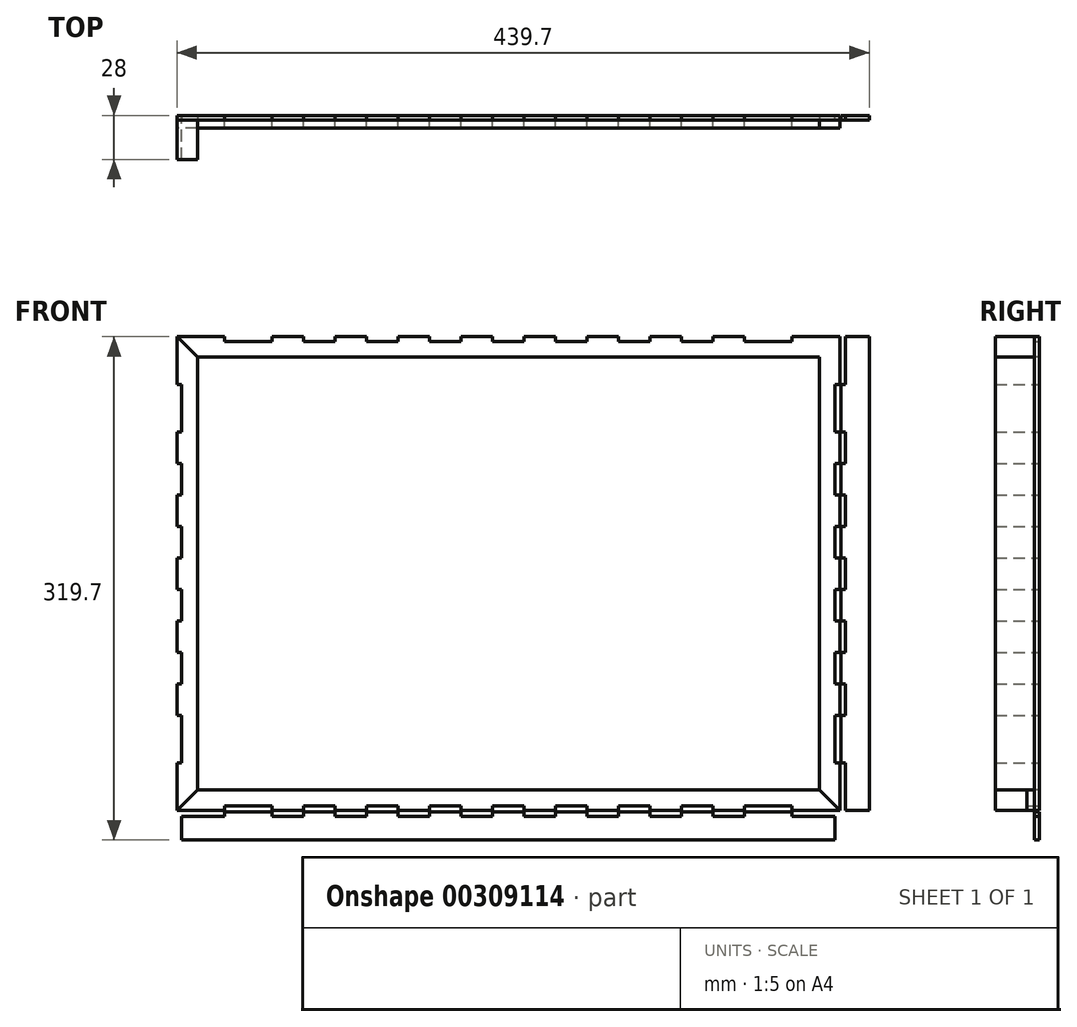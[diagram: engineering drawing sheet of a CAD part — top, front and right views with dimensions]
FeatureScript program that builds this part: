
annotation { "Feature Type Name" : "Feature", "Feature Type Description" : "" }
export const myFeature = defineFeature(function(context is Context, id is Id, definition is map)
    precondition{}
    {
        {
            var Q0;
            Q0=qCreatedBy(makeId("Front.planeOp"),FACE);
            var sketch = newSketch(context, id + "F0", { "sketchPlane" : qUnion([Q0])});
            skLineSegment(sketch, "E0", {"start": v(-313.85, 253.85) * mm, "end": v(-283.6, 253.85) * mm});
            skLineSegment(sketch, "E1", {"start": v(-283.6, 253.85) * mm, "end": v(-283.6, 250.85) * mm});
            skLineSegment(sketch, "E2", {"start": v(-283.6, 250.85) * mm, "end": v(-253.35, 250.85) * mm});
            skLineSegment(sketch, "E3", {"start": v(-253.35, 250.85) * mm, "end": v(-253.35, 253.85) * mm});
            skLineSegment(sketch, "E4", {"start": v(-253.35, 253.85) * mm, "end": v(-233.35, 253.85) * mm});
            skLineSegment(sketch, "E5", {"start": v(-233.35, 253.85) * mm, "end": v(-233.35, 250.85) * mm});
            skLineSegment(sketch, "E6", {"start": v(-233.35, 250.85) * mm, "end": v(-213.35, 250.85) * mm});
            skLineSegment(sketch, "E7", {"start": v(-213.35, 250.85) * mm, "end": v(-213.35, 253.85) * mm});
            skLineSegment(sketch, "E8", {"start": v(-213.35, 253.85) * mm, "end": v(-193.35, 253.85) * mm});
            skLineSegment(sketch, "E9", {"start": v(-193.35, 253.85) * mm, "end": v(-193.35, 250.85) * mm});
            skLineSegment(sketch, "E10", {"start": v(-193.35, 250.85) * mm, "end": v(-173.35, 250.85) * mm});
            skLineSegment(sketch, "E11", {"start": v(-173.35, 250.85) * mm, "end": v(-173.35, 253.85) * mm});
            skLineSegment(sketch, "E12", {"start": v(-173.35, 253.85) * mm, "end": v(-153.35, 253.85) * mm});
            skLineSegment(sketch, "E13", {"start": v(-153.35, 253.85) * mm, "end": v(-153.35, 250.85) * mm});
            skLineSegment(sketch, "E14", {"start": v(-153.35, 250.85) * mm, "end": v(-133.35, 250.85) * mm});
            skLineSegment(sketch, "E15", {"start": v(-133.35, 250.85) * mm, "end": v(-133.35, 253.85) * mm});
            skLineSegment(sketch, "E16", {"start": v(-133.35, 253.85) * mm, "end": v(-113.35, 253.85) * mm});
            skLineSegment(sketch, "E17", {"start": v(-113.35, 253.85) * mm, "end": v(-113.35, 250.85) * mm});
            skLineSegment(sketch, "E18", {"start": v(-113.35, 250.85) * mm, "end": v(-93.35, 250.85) * mm});
            skLineSegment(sketch, "E19", {"start": v(-93.35, 250.85) * mm, "end": v(-93.35, 253.85) * mm});
            skLineSegment(sketch, "E20", {"start": v(-93.35, 253.85) * mm, "end": v(-73.35, 253.85) * mm});
            skLineSegment(sketch, "E21", {"start": v(-73.35, 253.85) * mm, "end": v(-73.35, 250.85) * mm});
            skLineSegment(sketch, "E22", {"start": v(-73.35, 250.85) * mm, "end": v(-53.35, 250.85) * mm});
            skLineSegment(sketch, "E23", {"start": v(-53.35, 250.85) * mm, "end": v(-53.35, 253.85) * mm});
            skLineSegment(sketch, "E24", {"start": v(-53.35, 253.85) * mm, "end": v(-33.35, 253.85) * mm});
            skLineSegment(sketch, "E25", {"start": v(-33.35, 253.85) * mm, "end": v(-33.35, 250.85) * mm});
            skLineSegment(sketch, "E26", {"start": v(-33.35, 250.85) * mm, "end": v(-13.35, 250.85) * mm});
            skLineSegment(sketch, "E27", {"start": v(-13.35, 250.85) * mm, "end": v(-13.35, 253.85) * mm});
            skLineSegment(sketch, "E28", {"start": v(-13.35, 253.85) * mm, "end": v(6.65, 253.85) * mm});
            skLineSegment(sketch, "E29", {"start": v(6.65, 253.85) * mm, "end": v(6.65, 250.85) * mm});
            skLineSegment(sketch, "E30", {"start": v(6.65, 250.85) * mm, "end": v(26.65, 250.85) * mm});
            skLineSegment(sketch, "E31", {"start": v(26.65, 250.85) * mm, "end": v(26.65, 253.85) * mm});
            skLineSegment(sketch, "E32", {"start": v(26.65, 253.85) * mm, "end": v(46.65, 253.85) * mm});
            skLineSegment(sketch, "E33", {"start": v(46.65, 253.85) * mm, "end": v(46.65, 250.85) * mm});
            skLineSegment(sketch, "E34", {"start": v(46.65, 250.85) * mm, "end": v(76.9, 250.85) * mm});
            skLineSegment(sketch, "E35", {"start": v(76.9, 250.85) * mm, "end": v(76.9, 253.85) * mm});
            skLineSegment(sketch, "E36", {"start": v(76.9, 253.85) * mm, "end": v(107.15, 253.85) * mm});
            skLineSegment(sketch, "E37", {"start": v(107.15, 253.85) * mm, "end": v(107.15, 223.6) * mm});
            skLineSegment(sketch, "E38", {"start": v(107.15, 223.6) * mm, "end": v(104.15, 223.6) * mm});
            skLineSegment(sketch, "E39", {"start": v(104.15, 223.6) * mm, "end": v(104.15, 193.35) * mm});
            skLineSegment(sketch, "E40", {"start": v(104.15, 193.35) * mm, "end": v(107.15, 193.35) * mm});
            skLineSegment(sketch, "E41", {"start": v(107.15, 193.35) * mm, "end": v(107.15, 173.35) * mm});
            skLineSegment(sketch, "E42", {"start": v(107.15, 173.35) * mm, "end": v(104.15, 173.35) * mm});
            skLineSegment(sketch, "E43", {"start": v(104.15, 173.35) * mm, "end": v(104.15, 153.35) * mm});
            skLineSegment(sketch, "E44", {"start": v(104.15, 153.35) * mm, "end": v(107.15, 153.35) * mm});
            skLineSegment(sketch, "E45", {"start": v(107.15, 153.35) * mm, "end": v(107.15, 133.35) * mm});
            skLineSegment(sketch, "E46", {"start": v(107.15, 133.35) * mm, "end": v(104.15, 133.35) * mm});
            skLineSegment(sketch, "E47", {"start": v(104.15, 133.35) * mm, "end": v(104.15, 113.35) * mm});
            skLineSegment(sketch, "E48", {"start": v(104.15, 113.35) * mm, "end": v(107.15, 113.35) * mm});
            skLineSegment(sketch, "E49", {"start": v(107.15, 113.35) * mm, "end": v(107.15, 93.35) * mm});
            skLineSegment(sketch, "E50", {"start": v(107.15, 93.35) * mm, "end": v(104.15, 93.35) * mm});
            skLineSegment(sketch, "E51", {"start": v(104.15, 93.35) * mm, "end": v(104.15, 73.35) * mm});
            skLineSegment(sketch, "E52", {"start": v(104.15, 73.35) * mm, "end": v(107.15, 73.35) * mm});
            skLineSegment(sketch, "E53", {"start": v(107.15, 73.35) * mm, "end": v(107.15, 53.35) * mm});
            skLineSegment(sketch, "E54", {"start": v(107.15, 53.35) * mm, "end": v(104.15, 53.35) * mm});
            skLineSegment(sketch, "E55", {"start": v(104.15, 53.35) * mm, "end": v(104.15, 33.35) * mm});
            skLineSegment(sketch, "E56", {"start": v(104.15, 33.35) * mm, "end": v(107.15, 33.35) * mm});
            skLineSegment(sketch, "E57", {"start": v(107.15, 33.35) * mm, "end": v(107.15, 13.35) * mm});
            skLineSegment(sketch, "E58", {"start": v(107.15, 13.35) * mm, "end": v(104.15, 13.35) * mm});
            skLineSegment(sketch, "E59", {"start": v(104.15, 13.35) * mm, "end": v(104.15, -16.9) * mm});
            skLineSegment(sketch, "E60", {"start": v(104.15, -16.9) * mm, "end": v(107.15, -16.9) * mm});
            skLineSegment(sketch, "E61", {"start": v(107.15, -16.9) * mm, "end": v(107.15, -47.15) * mm});
            skLineSegment(sketch, "E62", {"start": v(107.15, -47.15) * mm, "end": v(76.9, -47.15) * mm});
            skLineSegment(sketch, "E63", {"start": v(76.9, -47.15) * mm, "end": v(76.9, -44.15) * mm});
            skLineSegment(sketch, "E64", {"start": v(76.9, -44.15) * mm, "end": v(46.65, -44.15) * mm});
            skLineSegment(sketch, "E65", {"start": v(46.65, -44.15) * mm, "end": v(46.65, -47.15) * mm});
            skLineSegment(sketch, "E66", {"start": v(46.65, -47.15) * mm, "end": v(26.65, -47.15) * mm});
            skLineSegment(sketch, "E67", {"start": v(26.65, -47.15) * mm, "end": v(26.65, -44.15) * mm});
            skLineSegment(sketch, "E68", {"start": v(26.65, -44.15) * mm, "end": v(6.65, -44.15) * mm});
            skLineSegment(sketch, "E69", {"start": v(6.65, -44.15) * mm, "end": v(6.65, -47.15) * mm});
            skLineSegment(sketch, "E70", {"start": v(6.65, -47.15) * mm, "end": v(-13.35, -47.15) * mm});
            skLineSegment(sketch, "E71", {"start": v(-13.35, -47.15) * mm, "end": v(-13.35, -44.15) * mm});
            skLineSegment(sketch, "E72", {"start": v(-13.35, -44.15) * mm, "end": v(-33.35, -44.15) * mm});
            skLineSegment(sketch, "E73", {"start": v(-33.35, -44.15) * mm, "end": v(-33.35, -47.15) * mm});
            skLineSegment(sketch, "E74", {"start": v(-33.35, -47.15) * mm, "end": v(-53.35, -47.15) * mm});
            skLineSegment(sketch, "E75", {"start": v(-53.35, -47.15) * mm, "end": v(-53.35, -44.15) * mm});
            skLineSegment(sketch, "E76", {"start": v(-53.35, -44.15) * mm, "end": v(-73.35, -44.15) * mm});
            skLineSegment(sketch, "E77", {"start": v(-73.35, -44.15) * mm, "end": v(-73.35, -47.15) * mm});
            skLineSegment(sketch, "E78", {"start": v(-73.35, -47.15) * mm, "end": v(-93.35, -47.15) * mm});
            skLineSegment(sketch, "E79", {"start": v(-93.35, -47.15) * mm, "end": v(-93.35, -44.15) * mm});
            skLineSegment(sketch, "E80", {"start": v(-93.35, -44.15) * mm, "end": v(-113.35, -44.15) * mm});
            skLineSegment(sketch, "E81", {"start": v(-113.35, -44.15) * mm, "end": v(-113.35, -47.15) * mm});
            skLineSegment(sketch, "E82", {"start": v(-113.35, -47.15) * mm, "end": v(-133.35, -47.15) * mm});
            skLineSegment(sketch, "E83", {"start": v(-133.35, -47.15) * mm, "end": v(-133.35, -44.15) * mm});
            skLineSegment(sketch, "E84", {"start": v(-133.35, -44.15) * mm, "end": v(-153.35, -44.15) * mm});
            skLineSegment(sketch, "E85", {"start": v(-153.35, -44.15) * mm, "end": v(-153.35, -47.15) * mm});
            skLineSegment(sketch, "E86", {"start": v(-153.35, -47.15) * mm, "end": v(-173.35, -47.15) * mm});
            skLineSegment(sketch, "E87", {"start": v(-173.35, -47.15) * mm, "end": v(-173.35, -44.15) * mm});
            skLineSegment(sketch, "E88", {"start": v(-173.35, -44.15) * mm, "end": v(-193.35, -44.15) * mm});
            skLineSegment(sketch, "E89", {"start": v(-193.35, -44.15) * mm, "end": v(-193.35, -47.15) * mm});
            skLineSegment(sketch, "E90", {"start": v(-193.35, -47.15) * mm, "end": v(-213.35, -47.15) * mm});
            skLineSegment(sketch, "E91", {"start": v(-213.35, -47.15) * mm, "end": v(-213.35, -44.15) * mm});
            skLineSegment(sketch, "E92", {"start": v(-213.35, -44.15) * mm, "end": v(-233.35, -44.15) * mm});
            skLineSegment(sketch, "E93", {"start": v(-233.35, -44.15) * mm, "end": v(-233.35, -47.15) * mm});
            skLineSegment(sketch, "E94", {"start": v(-233.35, -47.15) * mm, "end": v(-253.35, -47.15) * mm});
            skLineSegment(sketch, "E95", {"start": v(-253.35, -47.15) * mm, "end": v(-253.35, -44.15) * mm});
            skLineSegment(sketch, "E96", {"start": v(-253.35, -44.15) * mm, "end": v(-283.6, -44.15) * mm});
            skLineSegment(sketch, "E97", {"start": v(-283.6, -44.15) * mm, "end": v(-283.6, -47.15) * mm});
            skLineSegment(sketch, "E98", {"start": v(-283.6, -47.15) * mm, "end": v(-313.85, -47.15) * mm});
            skLineSegment(sketch, "E99", {"start": v(-313.85, -47.15) * mm, "end": v(-313.85, -16.9) * mm});
            skLineSegment(sketch, "E100", {"start": v(-313.85, -16.9) * mm, "end": v(-310.85, -16.9) * mm});
            skLineSegment(sketch, "E101", {"start": v(-310.85, -16.9) * mm, "end": v(-310.85, 13.35) * mm});
            skLineSegment(sketch, "E102", {"start": v(-310.85, 13.35) * mm, "end": v(-313.85, 13.35) * mm});
            skLineSegment(sketch, "E103", {"start": v(-313.85, 13.35) * mm, "end": v(-313.85, 33.35) * mm});
            skLineSegment(sketch, "E104", {"start": v(-313.85, 33.35) * mm, "end": v(-310.85, 33.35) * mm});
            skLineSegment(sketch, "E105", {"start": v(-310.85, 33.35) * mm, "end": v(-310.85, 53.35) * mm});
            skLineSegment(sketch, "E106", {"start": v(-310.85, 53.35) * mm, "end": v(-313.85, 53.35) * mm});
            skLineSegment(sketch, "E107", {"start": v(-313.85, 53.35) * mm, "end": v(-313.85, 73.35) * mm});
            skLineSegment(sketch, "E108", {"start": v(-313.85, 73.35) * mm, "end": v(-310.85, 73.35) * mm});
            skLineSegment(sketch, "E109", {"start": v(-310.85, 73.35) * mm, "end": v(-310.85, 93.35) * mm});
            skLineSegment(sketch, "E110", {"start": v(-310.85, 93.35) * mm, "end": v(-313.85, 93.35) * mm});
            skLineSegment(sketch, "E111", {"start": v(-313.85, 93.35) * mm, "end": v(-313.85, 113.35) * mm});
            skLineSegment(sketch, "E112", {"start": v(-313.85, 113.35) * mm, "end": v(-310.85, 113.35) * mm});
            skLineSegment(sketch, "E113", {"start": v(-310.85, 113.35) * mm, "end": v(-310.85, 133.35) * mm});
            skLineSegment(sketch, "E114", {"start": v(-310.85, 133.35) * mm, "end": v(-313.85, 133.35) * mm});
            skLineSegment(sketch, "E115", {"start": v(-313.85, 133.35) * mm, "end": v(-313.85, 153.35) * mm});
            skLineSegment(sketch, "E116", {"start": v(-313.85, 153.35) * mm, "end": v(-310.85, 153.35) * mm});
            skLineSegment(sketch, "E117", {"start": v(-310.85, 153.35) * mm, "end": v(-310.85, 173.35) * mm});
            skLineSegment(sketch, "E118", {"start": v(-310.85, 173.35) * mm, "end": v(-313.85, 173.35) * mm});
            skLineSegment(sketch, "E119", {"start": v(-313.85, 173.35) * mm, "end": v(-313.85, 193.35) * mm});
            skLineSegment(sketch, "E120", {"start": v(-313.85, 193.35) * mm, "end": v(-310.85, 193.35) * mm});
            skLineSegment(sketch, "E121", {"start": v(-310.85, 193.35) * mm, "end": v(-310.85, 223.6) * mm});
            skLineSegment(sketch, "E122", {"start": v(-310.85, 223.6) * mm, "end": v(-313.85, 223.6) * mm});
            skLineSegment(sketch, "E123", {"start": v(-313.85, 223.6) * mm, "end": v(-313.85, 253.85) * mm});
            skLineSegment(sketch, "E124", {"start": v(110.85, 253.85) * mm, "end": v(134.35, 253.85) * mm});
            skLineSegment(sketch, "E125", {"start": v(134.35, 253.85) * mm, "end": v(134.35, 250.85) * mm});
            skLineSegment(sketch, "E126", {"start": v(134.35, 250.85) * mm, "end": v(160.85, 250.85) * mm});
            skLineSegment(sketch, "E127", {"start": v(160.85, 250.85) * mm, "end": v(160.85, 253.85) * mm});
            skLineSegment(sketch, "E128", {"start": v(160.85, 253.85) * mm, "end": v(180.85, 253.85) * mm});
            skLineSegment(sketch, "E129", {"start": v(180.85, 253.85) * mm, "end": v(180.85, 250.85) * mm});
            skLineSegment(sketch, "E130", {"start": v(180.85, 250.85) * mm, "end": v(200.85, 250.85) * mm});
            skLineSegment(sketch, "E131", {"start": v(200.85, 250.85) * mm, "end": v(200.85, 253.85) * mm});
            skLineSegment(sketch, "E132", {"start": v(200.85, 253.85) * mm, "end": v(220.85, 253.85) * mm});
            skLineSegment(sketch, "E133", {"start": v(220.85, 253.85) * mm, "end": v(220.85, 250.85) * mm});
            skLineSegment(sketch, "E134", {"start": v(220.85, 250.85) * mm, "end": v(240.85, 250.85) * mm});
            skLineSegment(sketch, "E135", {"start": v(240.85, 250.85) * mm, "end": v(240.85, 253.85) * mm});
            skLineSegment(sketch, "E136", {"start": v(240.85, 253.85) * mm, "end": v(260.85, 253.85) * mm});
            skLineSegment(sketch, "E137", {"start": v(260.85, 253.85) * mm, "end": v(260.85, 250.85) * mm});
            skLineSegment(sketch, "E138", {"start": v(260.85, 250.85) * mm, "end": v(287.35, 250.85) * mm});
            skLineSegment(sketch, "E139", {"start": v(287.35, 250.85) * mm, "end": v(287.35, 253.85) * mm});
            skLineSegment(sketch, "E140", {"start": v(287.35, 253.85) * mm, "end": v(310.85, 253.85) * mm});
            skLineSegment(sketch, "E141", {"start": v(310.85, 253.85) * mm, "end": v(310.85, 223.6) * mm});
            skLineSegment(sketch, "E142", {"start": v(310.85, 223.6) * mm, "end": v(313.85, 223.6) * mm});
            skLineSegment(sketch, "E143", {"start": v(313.85, 223.6) * mm, "end": v(313.85, 193.35) * mm});
            skLineSegment(sketch, "E144", {"start": v(313.85, 193.35) * mm, "end": v(310.85, 193.35) * mm});
            skLineSegment(sketch, "E145", {"start": v(310.85, 193.35) * mm, "end": v(310.85, 173.35) * mm});
            skLineSegment(sketch, "E146", {"start": v(310.85, 173.35) * mm, "end": v(313.85, 173.35) * mm});
            skLineSegment(sketch, "E147", {"start": v(313.85, 173.35) * mm, "end": v(313.85, 153.35) * mm});
            skLineSegment(sketch, "E148", {"start": v(313.85, 153.35) * mm, "end": v(310.85, 153.35) * mm});
            skLineSegment(sketch, "E149", {"start": v(310.85, 153.35) * mm, "end": v(310.85, 133.35) * mm});
            skLineSegment(sketch, "E150", {"start": v(310.85, 133.35) * mm, "end": v(313.85, 133.35) * mm});
            skLineSegment(sketch, "E151", {"start": v(313.85, 133.35) * mm, "end": v(313.85, 113.35) * mm});
            skLineSegment(sketch, "E152", {"start": v(313.85, 113.35) * mm, "end": v(310.85, 113.35) * mm});
            skLineSegment(sketch, "E153", {"start": v(310.85, 113.35) * mm, "end": v(310.85, 93.35) * mm});
            skLineSegment(sketch, "E154", {"start": v(310.85, 93.35) * mm, "end": v(313.85, 93.35) * mm});
            skLineSegment(sketch, "E155", {"start": v(313.85, 93.35) * mm, "end": v(313.85, 73.35) * mm});
            skLineSegment(sketch, "E156", {"start": v(313.85, 73.35) * mm, "end": v(310.85, 73.35) * mm});
            skLineSegment(sketch, "E157", {"start": v(310.85, 73.35) * mm, "end": v(310.85, 53.35) * mm});
            skLineSegment(sketch, "E158", {"start": v(310.85, 53.35) * mm, "end": v(313.85, 53.35) * mm});
            skLineSegment(sketch, "E159", {"start": v(313.85, 53.35) * mm, "end": v(313.85, 33.35) * mm});
            skLineSegment(sketch, "E160", {"start": v(313.85, 33.35) * mm, "end": v(310.85, 33.35) * mm});
            skLineSegment(sketch, "E161", {"start": v(310.85, 33.35) * mm, "end": v(310.85, 13.35) * mm});
            skLineSegment(sketch, "E162", {"start": v(310.85, 13.35) * mm, "end": v(313.85, 13.35) * mm});
            skLineSegment(sketch, "E163", {"start": v(313.85, 13.35) * mm, "end": v(313.85, -16.9) * mm});
            skLineSegment(sketch, "E164", {"start": v(313.85, -16.9) * mm, "end": v(310.85, -16.9) * mm});
            skLineSegment(sketch, "E165", {"start": v(310.85, -16.9) * mm, "end": v(310.85, -47.15) * mm});
            skLineSegment(sketch, "E166", {"start": v(310.85, -47.15) * mm, "end": v(287.35, -47.15) * mm});
            skLineSegment(sketch, "E167", {"start": v(287.35, -47.15) * mm, "end": v(287.35, -44.15) * mm});
            skLineSegment(sketch, "E168", {"start": v(287.35, -44.15) * mm, "end": v(260.85, -44.15) * mm});
            skLineSegment(sketch, "E169", {"start": v(260.85, -44.15) * mm, "end": v(260.85, -47.15) * mm});
            skLineSegment(sketch, "E170", {"start": v(260.85, -47.15) * mm, "end": v(240.85, -47.15) * mm});
            skLineSegment(sketch, "E171", {"start": v(240.85, -47.15) * mm, "end": v(240.85, -44.15) * mm});
            skLineSegment(sketch, "E172", {"start": v(240.85, -44.15) * mm, "end": v(220.85, -44.15) * mm});
            skLineSegment(sketch, "E173", {"start": v(220.85, -44.15) * mm, "end": v(220.85, -47.15) * mm});
            skLineSegment(sketch, "E174", {"start": v(220.85, -47.15) * mm, "end": v(200.85, -47.15) * mm});
            skLineSegment(sketch, "E175", {"start": v(200.85, -47.15) * mm, "end": v(200.85, -44.15) * mm});
            skLineSegment(sketch, "E176", {"start": v(200.85, -44.15) * mm, "end": v(180.85, -44.15) * mm});
            skLineSegment(sketch, "E177", {"start": v(180.85, -44.15) * mm, "end": v(180.85, -47.15) * mm});
            skLineSegment(sketch, "E178", {"start": v(180.85, -47.15) * mm, "end": v(160.85, -47.15) * mm});
            skLineSegment(sketch, "E179", {"start": v(160.85, -47.15) * mm, "end": v(160.85, -44.15) * mm});
            skLineSegment(sketch, "E180", {"start": v(160.85, -44.15) * mm, "end": v(134.35, -44.15) * mm});
            skLineSegment(sketch, "E181", {"start": v(134.35, -44.15) * mm, "end": v(134.35, -47.15) * mm});
            skLineSegment(sketch, "E182", {"start": v(134.35, -47.15) * mm, "end": v(110.85, -47.15) * mm});
            skLineSegment(sketch, "E183", {"start": v(110.85, -47.15) * mm, "end": v(110.85, -16.9) * mm});
            skLineSegment(sketch, "E184", {"start": v(110.85, -16.9) * mm, "end": v(107.85, -16.9) * mm});
            skLineSegment(sketch, "E185", {"start": v(107.85, -16.9) * mm, "end": v(107.85, 13.35) * mm});
            skLineSegment(sketch, "E186", {"start": v(107.85, 13.35) * mm, "end": v(110.85, 13.35) * mm});
            skLineSegment(sketch, "E187", {"start": v(110.85, 13.35) * mm, "end": v(110.85, 33.35) * mm});
            skLineSegment(sketch, "E188", {"start": v(110.85, 33.35) * mm, "end": v(107.85, 33.35) * mm});
            skLineSegment(sketch, "E189", {"start": v(107.85, 33.35) * mm, "end": v(107.85, 53.35) * mm});
            skLineSegment(sketch, "E190", {"start": v(107.85, 53.35) * mm, "end": v(110.85, 53.35) * mm});
            skLineSegment(sketch, "E191", {"start": v(110.85, 53.35) * mm, "end": v(110.85, 73.35) * mm});
            skLineSegment(sketch, "E192", {"start": v(110.85, 73.35) * mm, "end": v(107.85, 73.35) * mm});
            skLineSegment(sketch, "E193", {"start": v(107.85, 73.35) * mm, "end": v(107.85, 93.35) * mm});
            skLineSegment(sketch, "E194", {"start": v(107.85, 93.35) * mm, "end": v(110.85, 93.35) * mm});
            skLineSegment(sketch, "E195", {"start": v(110.85, 93.35) * mm, "end": v(110.85, 113.35) * mm});
            skLineSegment(sketch, "E196", {"start": v(110.85, 113.35) * mm, "end": v(107.85, 113.35) * mm});
            skLineSegment(sketch, "E197", {"start": v(107.85, 113.35) * mm, "end": v(107.85, 133.35) * mm});
            skLineSegment(sketch, "E198", {"start": v(107.85, 133.35) * mm, "end": v(110.85, 133.35) * mm});
            skLineSegment(sketch, "E199", {"start": v(110.85, 133.35) * mm, "end": v(110.85, 153.35) * mm});
            skLineSegment(sketch, "E200", {"start": v(110.85, 153.35) * mm, "end": v(107.85, 153.35) * mm});
            skLineSegment(sketch, "E201", {"start": v(107.85, 153.35) * mm, "end": v(107.85, 173.35) * mm});
            skLineSegment(sketch, "E202", {"start": v(107.85, 173.35) * mm, "end": v(110.85, 173.35) * mm});
            skLineSegment(sketch, "E203", {"start": v(110.85, 173.35) * mm, "end": v(110.85, 193.35) * mm});
            skLineSegment(sketch, "E204", {"start": v(110.85, 193.35) * mm, "end": v(107.85, 193.35) * mm});
            skLineSegment(sketch, "E205", {"start": v(107.85, 193.35) * mm, "end": v(107.85, 223.6) * mm});
            skLineSegment(sketch, "E206", {"start": v(107.85, 223.6) * mm, "end": v(110.85, 223.6) * mm});
            skLineSegment(sketch, "E207", {"start": v(110.85, 223.6) * mm, "end": v(110.85, 253.85) * mm});
            skLineSegment(sketch, "E208", {"start": v(-310.85, -50.85) * mm, "end": v(-283.6, -50.85) * mm});
            skLineSegment(sketch, "E209", {"start": v(-283.6, -50.85) * mm, "end": v(-283.6, -47.85) * mm});
            skLineSegment(sketch, "E210", {"start": v(-283.6, -47.85) * mm, "end": v(-253.35, -47.85) * mm});
            skLineSegment(sketch, "E211", {"start": v(-253.35, -47.85) * mm, "end": v(-253.35, -50.85) * mm});
            skLineSegment(sketch, "E212", {"start": v(-253.35, -50.85) * mm, "end": v(-233.35, -50.85) * mm});
            skLineSegment(sketch, "E213", {"start": v(-233.35, -50.85) * mm, "end": v(-233.35, -47.85) * mm});
            skLineSegment(sketch, "E214", {"start": v(-233.35, -47.85) * mm, "end": v(-213.35, -47.85) * mm});
            skLineSegment(sketch, "E215", {"start": v(-213.35, -47.85) * mm, "end": v(-213.35, -50.85) * mm});
            skLineSegment(sketch, "E216", {"start": v(-213.35, -50.85) * mm, "end": v(-193.35, -50.85) * mm});
            skLineSegment(sketch, "E217", {"start": v(-193.35, -50.85) * mm, "end": v(-193.35, -47.85) * mm});
            skLineSegment(sketch, "E218", {"start": v(-193.35, -47.85) * mm, "end": v(-173.35, -47.85) * mm});
            skLineSegment(sketch, "E219", {"start": v(-173.35, -47.85) * mm, "end": v(-173.35, -50.85) * mm});
            skLineSegment(sketch, "E220", {"start": v(-173.35, -50.85) * mm, "end": v(-153.35, -50.85) * mm});
            skLineSegment(sketch, "E221", {"start": v(-153.35, -50.85) * mm, "end": v(-153.35, -47.85) * mm});
            skLineSegment(sketch, "E222", {"start": v(-153.35, -47.85) * mm, "end": v(-133.35, -47.85) * mm});
            skLineSegment(sketch, "E223", {"start": v(-133.35, -47.85) * mm, "end": v(-133.35, -50.85) * mm});
            skLineSegment(sketch, "E224", {"start": v(-133.35, -50.85) * mm, "end": v(-113.35, -50.85) * mm});
            skLineSegment(sketch, "E225", {"start": v(-113.35, -50.85) * mm, "end": v(-113.35, -47.85) * mm});
            skLineSegment(sketch, "E226", {"start": v(-113.35, -47.85) * mm, "end": v(-93.35, -47.85) * mm});
            skLineSegment(sketch, "E227", {"start": v(-93.35, -47.85) * mm, "end": v(-93.35, -50.85) * mm});
            skLineSegment(sketch, "E228", {"start": v(-93.35, -50.85) * mm, "end": v(-73.35, -50.85) * mm});
            skLineSegment(sketch, "E229", {"start": v(-73.35, -50.85) * mm, "end": v(-73.35, -47.85) * mm});
            skLineSegment(sketch, "E230", {"start": v(-73.35, -47.85) * mm, "end": v(-53.35, -47.85) * mm});
            skLineSegment(sketch, "E231", {"start": v(-53.35, -47.85) * mm, "end": v(-53.35, -50.85) * mm});
            skLineSegment(sketch, "E232", {"start": v(-53.35, -50.85) * mm, "end": v(-33.35, -50.85) * mm});
            skLineSegment(sketch, "E233", {"start": v(-33.35, -50.85) * mm, "end": v(-33.35, -47.85) * mm});
            skLineSegment(sketch, "E234", {"start": v(-33.35, -47.85) * mm, "end": v(-13.35, -47.85) * mm});
            skLineSegment(sketch, "E235", {"start": v(-13.35, -47.85) * mm, "end": v(-13.35, -50.85) * mm});
            skLineSegment(sketch, "E236", {"start": v(-13.35, -50.85) * mm, "end": v(6.65, -50.85) * mm});
            skLineSegment(sketch, "E237", {"start": v(6.65, -50.85) * mm, "end": v(6.65, -47.85) * mm});
            skLineSegment(sketch, "E238", {"start": v(6.65, -47.85) * mm, "end": v(26.65, -47.85) * mm});
            skLineSegment(sketch, "E239", {"start": v(26.65, -47.85) * mm, "end": v(26.65, -50.85) * mm});
            skLineSegment(sketch, "E240", {"start": v(26.65, -50.85) * mm, "end": v(46.65, -50.85) * mm});
            skLineSegment(sketch, "E241", {"start": v(46.65, -50.85) * mm, "end": v(46.65, -47.85) * mm});
            skLineSegment(sketch, "E242", {"start": v(46.65, -47.85) * mm, "end": v(76.9, -47.85) * mm});
            skLineSegment(sketch, "E243", {"start": v(76.9, -47.85) * mm, "end": v(76.9, -50.85) * mm});
            skLineSegment(sketch, "E244", {"start": v(76.9, -50.85) * mm, "end": v(104.15, -50.85) * mm});
            skLineSegment(sketch, "E245", {"start": v(104.15, -50.85) * mm, "end": v(104.15, -74.35) * mm});
            skLineSegment(sketch, "E246", {"start": v(104.15, -74.35) * mm, "end": v(107.15, -74.35) * mm});
            skLineSegment(sketch, "E247", {"start": v(107.15, -74.35) * mm, "end": v(107.15, -100.85) * mm});
            skLineSegment(sketch, "E248", {"start": v(107.15, -100.85) * mm, "end": v(104.15, -100.85) * mm});
            skLineSegment(sketch, "E249", {"start": v(104.15, -100.85) * mm, "end": v(104.15, -120.85) * mm});
            skLineSegment(sketch, "E250", {"start": v(104.15, -120.85) * mm, "end": v(107.15, -120.85) * mm});
            skLineSegment(sketch, "E251", {"start": v(107.15, -120.85) * mm, "end": v(107.15, -140.85) * mm});
            skLineSegment(sketch, "E252", {"start": v(107.15, -140.85) * mm, "end": v(104.15, -140.85) * mm});
            skLineSegment(sketch, "E253", {"start": v(104.15, -140.85) * mm, "end": v(104.15, -160.85) * mm});
            skLineSegment(sketch, "E254", {"start": v(104.15, -160.85) * mm, "end": v(107.15, -160.85) * mm});
            skLineSegment(sketch, "E255", {"start": v(107.15, -160.85) * mm, "end": v(107.15, -180.85) * mm});
            skLineSegment(sketch, "E256", {"start": v(107.15, -180.85) * mm, "end": v(104.15, -180.85) * mm});
            skLineSegment(sketch, "E257", {"start": v(104.15, -180.85) * mm, "end": v(104.15, -200.85) * mm});
            skLineSegment(sketch, "E258", {"start": v(104.15, -200.85) * mm, "end": v(107.15, -200.85) * mm});
            skLineSegment(sketch, "E259", {"start": v(107.15, -200.85) * mm, "end": v(107.15, -227.35) * mm});
            skLineSegment(sketch, "E260", {"start": v(107.15, -227.35) * mm, "end": v(104.15, -227.35) * mm});
            skLineSegment(sketch, "E261", {"start": v(104.15, -227.35) * mm, "end": v(104.15, -250.85) * mm});
            skLineSegment(sketch, "E262", {"start": v(104.15, -250.85) * mm, "end": v(76.9, -250.85) * mm});
            skLineSegment(sketch, "E263", {"start": v(76.9, -250.85) * mm, "end": v(76.9, -253.85) * mm});
            skLineSegment(sketch, "E264", {"start": v(76.9, -253.85) * mm, "end": v(46.65, -253.85) * mm});
            skLineSegment(sketch, "E265", {"start": v(46.65, -253.85) * mm, "end": v(46.65, -250.85) * mm});
            skLineSegment(sketch, "E266", {"start": v(46.65, -250.85) * mm, "end": v(26.65, -250.85) * mm});
            skLineSegment(sketch, "E267", {"start": v(26.65, -250.85) * mm, "end": v(26.65, -253.85) * mm});
            skLineSegment(sketch, "E268", {"start": v(26.65, -253.85) * mm, "end": v(6.65, -253.85) * mm});
            skLineSegment(sketch, "E269", {"start": v(6.65, -253.85) * mm, "end": v(6.65, -250.85) * mm});
            skLineSegment(sketch, "E270", {"start": v(6.65, -250.85) * mm, "end": v(-13.35, -250.85) * mm});
            skLineSegment(sketch, "E271", {"start": v(-13.35, -250.85) * mm, "end": v(-13.35, -253.85) * mm});
            skLineSegment(sketch, "E272", {"start": v(-13.35, -253.85) * mm, "end": v(-33.35, -253.85) * mm});
            skLineSegment(sketch, "E273", {"start": v(-33.35, -253.85) * mm, "end": v(-33.35, -250.85) * mm});
            skLineSegment(sketch, "E274", {"start": v(-33.35, -250.85) * mm, "end": v(-53.35, -250.85) * mm});
            skLineSegment(sketch, "E275", {"start": v(-53.35, -250.85) * mm, "end": v(-53.35, -253.85) * mm});
            skLineSegment(sketch, "E276", {"start": v(-53.35, -253.85) * mm, "end": v(-73.35, -253.85) * mm});
            skLineSegment(sketch, "E277", {"start": v(-73.35, -253.85) * mm, "end": v(-73.35, -250.85) * mm});
            skLineSegment(sketch, "E278", {"start": v(-73.35, -250.85) * mm, "end": v(-93.35, -250.85) * mm});
            skLineSegment(sketch, "E279", {"start": v(-93.35, -250.85) * mm, "end": v(-93.35, -253.85) * mm});
            skLineSegment(sketch, "E280", {"start": v(-93.35, -253.85) * mm, "end": v(-113.35, -253.85) * mm});
            skLineSegment(sketch, "E281", {"start": v(-113.35, -253.85) * mm, "end": v(-113.35, -250.85) * mm});
            skLineSegment(sketch, "E282", {"start": v(-113.35, -250.85) * mm, "end": v(-133.35, -250.85) * mm});
            skLineSegment(sketch, "E283", {"start": v(-133.35, -250.85) * mm, "end": v(-133.35, -253.85) * mm});
            skLineSegment(sketch, "E284", {"start": v(-133.35, -253.85) * mm, "end": v(-153.35, -253.85) * mm});
            skLineSegment(sketch, "E285", {"start": v(-153.35, -253.85) * mm, "end": v(-153.35, -250.85) * mm});
            skLineSegment(sketch, "E286", {"start": v(-153.35, -250.85) * mm, "end": v(-173.35, -250.85) * mm});
            skLineSegment(sketch, "E287", {"start": v(-173.35, -250.85) * mm, "end": v(-173.35, -253.85) * mm});
            skLineSegment(sketch, "E288", {"start": v(-173.35, -253.85) * mm, "end": v(-193.35, -253.85) * mm});
            skLineSegment(sketch, "E289", {"start": v(-193.35, -253.85) * mm, "end": v(-193.35, -250.85) * mm});
            skLineSegment(sketch, "E290", {"start": v(-193.35, -250.85) * mm, "end": v(-213.35, -250.85) * mm});
            skLineSegment(sketch, "E291", {"start": v(-213.35, -250.85) * mm, "end": v(-213.35, -253.85) * mm});
            skLineSegment(sketch, "E292", {"start": v(-213.35, -253.85) * mm, "end": v(-233.35, -253.85) * mm});
            skLineSegment(sketch, "E293", {"start": v(-233.35, -253.85) * mm, "end": v(-233.35, -250.85) * mm});
            skLineSegment(sketch, "E294", {"start": v(-233.35, -250.85) * mm, "end": v(-253.35, -250.85) * mm});
            skLineSegment(sketch, "E295", {"start": v(-253.35, -250.85) * mm, "end": v(-253.35, -253.85) * mm});
            skLineSegment(sketch, "E296", {"start": v(-253.35, -253.85) * mm, "end": v(-283.6, -253.85) * mm});
            skLineSegment(sketch, "E297", {"start": v(-283.6, -253.85) * mm, "end": v(-283.6, -250.85) * mm});
            skLineSegment(sketch, "E298", {"start": v(-283.6, -250.85) * mm, "end": v(-310.85, -250.85) * mm});
            skLineSegment(sketch, "E299", {"start": v(-310.85, -250.85) * mm, "end": v(-310.85, -227.35) * mm});
            skLineSegment(sketch, "E300", {"start": v(-310.85, -227.35) * mm, "end": v(-313.85, -227.35) * mm});
            skLineSegment(sketch, "E301", {"start": v(-313.85, -227.35) * mm, "end": v(-313.85, -200.85) * mm});
            skLineSegment(sketch, "E302", {"start": v(-313.85, -200.85) * mm, "end": v(-310.85, -200.85) * mm});
            skLineSegment(sketch, "E303", {"start": v(-310.85, -200.85) * mm, "end": v(-310.85, -180.85) * mm});
            skLineSegment(sketch, "E304", {"start": v(-310.85, -180.85) * mm, "end": v(-313.85, -180.85) * mm});
            skLineSegment(sketch, "E305", {"start": v(-313.85, -180.85) * mm, "end": v(-313.85, -160.85) * mm});
            skLineSegment(sketch, "E306", {"start": v(-313.85, -160.85) * mm, "end": v(-310.85, -160.85) * mm});
            skLineSegment(sketch, "E307", {"start": v(-310.85, -160.85) * mm, "end": v(-310.85, -140.85) * mm});
            skLineSegment(sketch, "E308", {"start": v(-310.85, -140.85) * mm, "end": v(-313.85, -140.85) * mm});
            skLineSegment(sketch, "E309", {"start": v(-313.85, -140.85) * mm, "end": v(-313.85, -120.85) * mm});
            skLineSegment(sketch, "E310", {"start": v(-313.85, -120.85) * mm, "end": v(-310.85, -120.85) * mm});
            skLineSegment(sketch, "E311", {"start": v(-310.85, -120.85) * mm, "end": v(-310.85, -100.85) * mm});
            skLineSegment(sketch, "E312", {"start": v(-310.85, -100.85) * mm, "end": v(-313.85, -100.85) * mm});
            skLineSegment(sketch, "E313", {"start": v(-313.85, -100.85) * mm, "end": v(-313.85, -74.35) * mm});
            skLineSegment(sketch, "E314", {"start": v(-313.85, -74.35) * mm, "end": v(-310.85, -74.35) * mm});
            skLineSegment(sketch, "E315", {"start": v(-310.85, -74.35) * mm, "end": v(-310.85, -50.85) * mm});
            skSolve(sketch);
        }
        {
            var Q0;
            Q0 = qSketchRegion(id + "F0", true);
            extrude(context, id + "F1", {"entities" : qUnion([Q0]), "depth" : 3 * mm});
        }
        {
            var Q0;
            Q0=makeQuery(id+"F1.opExtrude","CAP_FACE",FACE,{"disambiguationData":[OSD([sQuery(id+"F0.wireOp",EDGE,"E0"),sQuery(id+"F0.wireOp",EDGE,"E1"),sQuery(id+"F0.wireOp",EDGE,"E2"),sQuery(id+"F0.wireOp",EDGE,"E3"),sQuery(id+"F0.wireOp",EDGE,"E4"),sQuery(id+"F0.wireOp",EDGE,"E5"),sQuery(id+"F0.wireOp",EDGE,"E6"),sQuery(id+"F0.wireOp",EDGE,"E7"),sQuery(id+"F0.wireOp",EDGE,"E8"),sQuery(id+"F0.wireOp",EDGE,"E9"),sQuery(id+"F0.wireOp",EDGE,"E10"),sQuery(id+"F0.wireOp",EDGE,"E11"),sQuery(id+"F0.wireOp",EDGE,"E12"),sQuery(id+"F0.wireOp",EDGE,"E13"),sQuery(id+"F0.wireOp",EDGE,"E14"),sQuery(id+"F0.wireOp",EDGE,"E15"),sQuery(id+"F0.wireOp",EDGE,"E16"),sQuery(id+"F0.wireOp",EDGE,"E17"),sQuery(id+"F0.wireOp",EDGE,"E18"),sQuery(id+"F0.wireOp",EDGE,"E19"),sQuery(id+"F0.wireOp",EDGE,"E20"),sQuery(id+"F0.wireOp",EDGE,"E21"),sQuery(id+"F0.wireOp",EDGE,"E22"),sQuery(id+"F0.wireOp",EDGE,"E23"),sQuery(id+"F0.wireOp",EDGE,"E24"),sQuery(id+"F0.wireOp",EDGE,"E25"),sQuery(id+"F0.wireOp",EDGE,"E26"),sQuery(id+"F0.wireOp",EDGE,"E27"),sQuery(id+"F0.wireOp",EDGE,"E28"),sQuery(id+"F0.wireOp",EDGE,"E29"),sQuery(id+"F0.wireOp",EDGE,"E30"),sQuery(id+"F0.wireOp",EDGE,"E31"),sQuery(id+"F0.wireOp",EDGE,"E32"),sQuery(id+"F0.wireOp",EDGE,"E33"),sQuery(id+"F0.wireOp",EDGE,"E34"),sQuery(id+"F0.wireOp",EDGE,"E35"),sQuery(id+"F0.wireOp",EDGE,"E36"),sQuery(id+"F0.wireOp",EDGE,"E37"),sQuery(id+"F0.wireOp",EDGE,"E38"),sQuery(id+"F0.wireOp",EDGE,"E39"),sQuery(id+"F0.wireOp",EDGE,"E40"),sQuery(id+"F0.wireOp",EDGE,"E41"),sQuery(id+"F0.wireOp",EDGE,"E42"),sQuery(id+"F0.wireOp",EDGE,"E43"),sQuery(id+"F0.wireOp",EDGE,"E44"),sQuery(id+"F0.wireOp",EDGE,"E45"),sQuery(id+"F0.wireOp",EDGE,"E46"),sQuery(id+"F0.wireOp",EDGE,"E47"),sQuery(id+"F0.wireOp",EDGE,"E48"),sQuery(id+"F0.wireOp",EDGE,"E49"),sQuery(id+"F0.wireOp",EDGE,"E50"),sQuery(id+"F0.wireOp",EDGE,"E51"),sQuery(id+"F0.wireOp",EDGE,"E52"),sQuery(id+"F0.wireOp",EDGE,"E53"),sQuery(id+"F0.wireOp",EDGE,"E54"),sQuery(id+"F0.wireOp",EDGE,"E55"),sQuery(id+"F0.wireOp",EDGE,"E56"),sQuery(id+"F0.wireOp",EDGE,"E57"),sQuery(id+"F0.wireOp",EDGE,"E58"),sQuery(id+"F0.wireOp",EDGE,"E59"),sQuery(id+"F0.wireOp",EDGE,"E60"),sQuery(id+"F0.wireOp",EDGE,"E61"),sQuery(id+"F0.wireOp",EDGE,"E62"),sQuery(id+"F0.wireOp",EDGE,"E63"),sQuery(id+"F0.wireOp",EDGE,"E64"),sQuery(id+"F0.wireOp",EDGE,"E65"),sQuery(id+"F0.wireOp",EDGE,"E66"),sQuery(id+"F0.wireOp",EDGE,"E67"),sQuery(id+"F0.wireOp",EDGE,"E68"),sQuery(id+"F0.wireOp",EDGE,"E69"),sQuery(id+"F0.wireOp",EDGE,"E70"),sQuery(id+"F0.wireOp",EDGE,"E71"),sQuery(id+"F0.wireOp",EDGE,"E72"),sQuery(id+"F0.wireOp",EDGE,"E73"),sQuery(id+"F0.wireOp",EDGE,"E74"),sQuery(id+"F0.wireOp",EDGE,"E75"),sQuery(id+"F0.wireOp",EDGE,"E76"),sQuery(id+"F0.wireOp",EDGE,"E77"),sQuery(id+"F0.wireOp",EDGE,"E78"),sQuery(id+"F0.wireOp",EDGE,"E79"),sQuery(id+"F0.wireOp",EDGE,"E80"),sQuery(id+"F0.wireOp",EDGE,"E81"),sQuery(id+"F0.wireOp",EDGE,"E82"),sQuery(id+"F0.wireOp",EDGE,"E83"),sQuery(id+"F0.wireOp",EDGE,"E84"),sQuery(id+"F0.wireOp",EDGE,"E85"),sQuery(id+"F0.wireOp",EDGE,"E86"),sQuery(id+"F0.wireOp",EDGE,"E87"),sQuery(id+"F0.wireOp",EDGE,"E88"),sQuery(id+"F0.wireOp",EDGE,"E89"),sQuery(id+"F0.wireOp",EDGE,"E90"),sQuery(id+"F0.wireOp",EDGE,"E91"),sQuery(id+"F0.wireOp",EDGE,"E92"),sQuery(id+"F0.wireOp",EDGE,"E93"),sQuery(id+"F0.wireOp",EDGE,"E94"),sQuery(id+"F0.wireOp",EDGE,"E95"),sQuery(id+"F0.wireOp",EDGE,"E96"),sQuery(id+"F0.wireOp",EDGE,"E97"),sQuery(id+"F0.wireOp",EDGE,"E98"),sQuery(id+"F0.wireOp",EDGE,"E99"),sQuery(id+"F0.wireOp",EDGE,"E100"),sQuery(id+"F0.wireOp",EDGE,"E101"),sQuery(id+"F0.wireOp",EDGE,"E102"),sQuery(id+"F0.wireOp",EDGE,"E103"),sQuery(id+"F0.wireOp",EDGE,"E104"),sQuery(id+"F0.wireOp",EDGE,"E105"),sQuery(id+"F0.wireOp",EDGE,"E106"),sQuery(id+"F0.wireOp",EDGE,"E107"),sQuery(id+"F0.wireOp",EDGE,"E108"),sQuery(id+"F0.wireOp",EDGE,"E109"),sQuery(id+"F0.wireOp",EDGE,"E110"),sQuery(id+"F0.wireOp",EDGE,"E111"),sQuery(id+"F0.wireOp",EDGE,"E112"),sQuery(id+"F0.wireOp",EDGE,"E113"),sQuery(id+"F0.wireOp",EDGE,"E114"),sQuery(id+"F0.wireOp",EDGE,"E115"),sQuery(id+"F0.wireOp",EDGE,"E116"),sQuery(id+"F0.wireOp",EDGE,"E117"),sQuery(id+"F0.wireOp",EDGE,"E118"),sQuery(id+"F0.wireOp",EDGE,"E119"),sQuery(id+"F0.wireOp",EDGE,"E120"),sQuery(id+"F0.wireOp",EDGE,"E121"),sQuery(id+"F0.wireOp",EDGE,"E122"),sQuery(id+"F0.wireOp",EDGE,"E123")])],"isStart":false});
            var sketch = newSketch(context, id + "F2", { "sketchPlane" : qUnion([Q0])});
            skLineSegment(sketch, "E316.bottom", {"start": v(-300.85, 240.85) * mm, "end": v(94.15, 240.85) * mm});
            skLineSegment(sketch, "E316.top", {"start": v(-300.85, -34.15) * mm, "end": v(94.15, -34.15) * mm});
            skLineSegment(sketch, "E316.left", {"start": v(-300.85, 240.85) * mm, "end": v(-300.85, -34.15) * mm});
            skLineSegment(sketch, "E316.right", {"start": v(94.15, 240.85) * mm, "end": v(94.15, -34.15) * mm});
            skLineSegment(sketch, "E317", {"start": v(-183.35, 250.85) * mm, "end": v(-183.35, 240.85) * mm, "construction": true});
            skLineSegment(sketch, "E318", {"start": v(-310.85, 123.35) * mm, "end": v(-300.85, 123.35) * mm, "construction": true});
            skLineSegment(sketch, "E319", {"start": v(-183.35, -44.15) * mm, "end": v(-183.35, -34.15) * mm, "construction": true});
            skLineSegment(sketch, "E320", {"start": v(104.15, 123.35) * mm, "end": v(94.15, 123.35) * mm, "construction": true});
            skLineSegment(sketch, "E321.bottom", {"start": v(313.85, 253.85) * mm, "end": v(125.85, 253.85) * mm});
            skLineSegment(sketch, "E321.top", {"start": v(313.85, -47.15) * mm, "end": v(125.85, -47.15) * mm});
            skLineSegment(sketch, "E321.left", {"start": v(313.85, 253.85) * mm, "end": v(313.85, -47.15) * mm});
            skLineSegment(sketch, "E321.right", {"start": v(125.85, 253.85) * mm, "end": v(125.85, -47.15) * mm});
            skLineSegment(sketch, "E322.bottom", {"start": v(-313.85, -253.85) * mm, "end": v(107.15, -253.85) * mm});
            skLineSegment(sketch, "E322.top", {"start": v(-313.85, -65.85) * mm, "end": v(107.15, -65.85) * mm});
            skLineSegment(sketch, "E322.left", {"start": v(-313.85, -253.85) * mm, "end": v(-313.85, -65.85) * mm});
            skLineSegment(sketch, "E322.right", {"start": v(107.15, -253.85) * mm, "end": v(107.15, -65.85) * mm});
            skLineSegment(sketch, "E323", {"start": v(125.85, 20.75) * mm, "end": v(110.85, 20.75) * mm, "construction": true});
            skLineSegment(sketch, "E324", {"start": v(39.3, -65.85) * mm, "end": v(39.3, -50.85) * mm, "construction": true});
            skSolve(sketch);
        }
        {
            var Q0;
            Q0 = qSketchRegion(id + "F2", true);
            extrude(context, id + "F3", {"entities" : qUnion([Q0]), "operationType" : NewBodyOperationType.REMOVE, "oppositeDirection" : true, "depth" : 25 * mm});
        }
        {
            var Q0;
            Q0=makeQuery(id+"F1.opExtrude","CAP_FACE",FACE,{"disambiguationData":[OSD([sQuery(id+"F0.wireOp",EDGE,"E0"),sQuery(id+"F0.wireOp",EDGE,"E1"),sQuery(id+"F0.wireOp",EDGE,"E2"),sQuery(id+"F0.wireOp",EDGE,"E3"),sQuery(id+"F0.wireOp",EDGE,"E4"),sQuery(id+"F0.wireOp",EDGE,"E5"),sQuery(id+"F0.wireOp",EDGE,"E6"),sQuery(id+"F0.wireOp",EDGE,"E7"),sQuery(id+"F0.wireOp",EDGE,"E8"),sQuery(id+"F0.wireOp",EDGE,"E9"),sQuery(id+"F0.wireOp",EDGE,"E10"),sQuery(id+"F0.wireOp",EDGE,"E11"),sQuery(id+"F0.wireOp",EDGE,"E12"),sQuery(id+"F0.wireOp",EDGE,"E13"),sQuery(id+"F0.wireOp",EDGE,"E14"),sQuery(id+"F0.wireOp",EDGE,"E15"),sQuery(id+"F0.wireOp",EDGE,"E16"),sQuery(id+"F0.wireOp",EDGE,"E17"),sQuery(id+"F0.wireOp",EDGE,"E18"),sQuery(id+"F0.wireOp",EDGE,"E19"),sQuery(id+"F0.wireOp",EDGE,"E20"),sQuery(id+"F0.wireOp",EDGE,"E21"),sQuery(id+"F0.wireOp",EDGE,"E22"),sQuery(id+"F0.wireOp",EDGE,"E23"),sQuery(id+"F0.wireOp",EDGE,"E24"),sQuery(id+"F0.wireOp",EDGE,"E25"),sQuery(id+"F0.wireOp",EDGE,"E26"),sQuery(id+"F0.wireOp",EDGE,"E27"),sQuery(id+"F0.wireOp",EDGE,"E28"),sQuery(id+"F0.wireOp",EDGE,"E29"),sQuery(id+"F0.wireOp",EDGE,"E30"),sQuery(id+"F0.wireOp",EDGE,"E31"),sQuery(id+"F0.wireOp",EDGE,"E32"),sQuery(id+"F0.wireOp",EDGE,"E33"),sQuery(id+"F0.wireOp",EDGE,"E34"),sQuery(id+"F0.wireOp",EDGE,"E35"),sQuery(id+"F0.wireOp",EDGE,"E36"),sQuery(id+"F0.wireOp",EDGE,"E37"),sQuery(id+"F0.wireOp",EDGE,"E38"),sQuery(id+"F0.wireOp",EDGE,"E39"),sQuery(id+"F0.wireOp",EDGE,"E40"),sQuery(id+"F0.wireOp",EDGE,"E41"),sQuery(id+"F0.wireOp",EDGE,"E42"),sQuery(id+"F0.wireOp",EDGE,"E43"),sQuery(id+"F0.wireOp",EDGE,"E44"),sQuery(id+"F0.wireOp",EDGE,"E45"),sQuery(id+"F0.wireOp",EDGE,"E46"),sQuery(id+"F0.wireOp",EDGE,"E47"),sQuery(id+"F0.wireOp",EDGE,"E48"),sQuery(id+"F0.wireOp",EDGE,"E49"),sQuery(id+"F0.wireOp",EDGE,"E50"),sQuery(id+"F0.wireOp",EDGE,"E51"),sQuery(id+"F0.wireOp",EDGE,"E52"),sQuery(id+"F0.wireOp",EDGE,"E53"),sQuery(id+"F0.wireOp",EDGE,"E54"),sQuery(id+"F0.wireOp",EDGE,"E55"),sQuery(id+"F0.wireOp",EDGE,"E56"),sQuery(id+"F0.wireOp",EDGE,"E57"),sQuery(id+"F0.wireOp",EDGE,"E58"),sQuery(id+"F0.wireOp",EDGE,"E59"),sQuery(id+"F0.wireOp",EDGE,"E60"),sQuery(id+"F0.wireOp",EDGE,"E61"),sQuery(id+"F0.wireOp",EDGE,"E62"),sQuery(id+"F0.wireOp",EDGE,"E63"),sQuery(id+"F0.wireOp",EDGE,"E64"),sQuery(id+"F0.wireOp",EDGE,"E65"),sQuery(id+"F0.wireOp",EDGE,"E66"),sQuery(id+"F0.wireOp",EDGE,"E67"),sQuery(id+"F0.wireOp",EDGE,"E68"),sQuery(id+"F0.wireOp",EDGE,"E69"),sQuery(id+"F0.wireOp",EDGE,"E70"),sQuery(id+"F0.wireOp",EDGE,"E71"),sQuery(id+"F0.wireOp",EDGE,"E72"),sQuery(id+"F0.wireOp",EDGE,"E73"),sQuery(id+"F0.wireOp",EDGE,"E74"),sQuery(id+"F0.wireOp",EDGE,"E75"),sQuery(id+"F0.wireOp",EDGE,"E76"),sQuery(id+"F0.wireOp",EDGE,"E77"),sQuery(id+"F0.wireOp",EDGE,"E78"),sQuery(id+"F0.wireOp",EDGE,"E79"),sQuery(id+"F0.wireOp",EDGE,"E80"),sQuery(id+"F0.wireOp",EDGE,"E81"),sQuery(id+"F0.wireOp",EDGE,"E82"),sQuery(id+"F0.wireOp",EDGE,"E83"),sQuery(id+"F0.wireOp",EDGE,"E84"),sQuery(id+"F0.wireOp",EDGE,"E85"),sQuery(id+"F0.wireOp",EDGE,"E86"),sQuery(id+"F0.wireOp",EDGE,"E87"),sQuery(id+"F0.wireOp",EDGE,"E88"),sQuery(id+"F0.wireOp",EDGE,"E89"),sQuery(id+"F0.wireOp",EDGE,"E90"),sQuery(id+"F0.wireOp",EDGE,"E91"),sQuery(id+"F0.wireOp",EDGE,"E92"),sQuery(id+"F0.wireOp",EDGE,"E93"),sQuery(id+"F0.wireOp",EDGE,"E94"),sQuery(id+"F0.wireOp",EDGE,"E95"),sQuery(id+"F0.wireOp",EDGE,"E96"),sQuery(id+"F0.wireOp",EDGE,"E97"),sQuery(id+"F0.wireOp",EDGE,"E98"),sQuery(id+"F0.wireOp",EDGE,"E99"),sQuery(id+"F0.wireOp",EDGE,"E100"),sQuery(id+"F0.wireOp",EDGE,"E101"),sQuery(id+"F0.wireOp",EDGE,"E102"),sQuery(id+"F0.wireOp",EDGE,"E103"),sQuery(id+"F0.wireOp",EDGE,"E104"),sQuery(id+"F0.wireOp",EDGE,"E105"),sQuery(id+"F0.wireOp",EDGE,"E106"),sQuery(id+"F0.wireOp",EDGE,"E107"),sQuery(id+"F0.wireOp",EDGE,"E108"),sQuery(id+"F0.wireOp",EDGE,"E109"),sQuery(id+"F0.wireOp",EDGE,"E110"),sQuery(id+"F0.wireOp",EDGE,"E111"),sQuery(id+"F0.wireOp",EDGE,"E112"),sQuery(id+"F0.wireOp",EDGE,"E113"),sQuery(id+"F0.wireOp",EDGE,"E114"),sQuery(id+"F0.wireOp",EDGE,"E115"),sQuery(id+"F0.wireOp",EDGE,"E116"),sQuery(id+"F0.wireOp",EDGE,"E117"),sQuery(id+"F0.wireOp",EDGE,"E118"),sQuery(id+"F0.wireOp",EDGE,"E119"),sQuery(id+"F0.wireOp",EDGE,"E120"),sQuery(id+"F0.wireOp",EDGE,"E121"),sQuery(id+"F0.wireOp",EDGE,"E122"),sQuery(id+"F0.wireOp",EDGE,"E123")])],"isStart":false});
            var sketch = newSketch(context, id + "F4", { "sketchPlane" : qUnion([Q0])});
            skLineSegment(sketch, "E325", {"start": v(-300.85, -34.15) * mm, "end": v(-313.85, -47.15) * mm});
            skLineSegment(sketch, "E326", {"start": v(-313.85, 253.85) * mm, "end": v(-300.85, 240.85) * mm});
            skSolve(sketch);
        }
        {
            var Q0;
            Q0=makeQuery(id+"F4.imprint","IMPRINT",FACE,{"disambiguationData":[TD([[makeQuery(id+"F4.imprint","IMPRINT",EDGE,{"derivedFrom":sQuery(id+"F4.wireOp",EDGE,"E325")}),-1.0]])]});
            extrude(context, id + "F5", {"entities" : qUnion([Q0]), "operationType" : NewBodyOperationType.ADD, "depth" : 25 * mm});
        }
        {
            var Q0;
            Q0=makeQuery(id+"F1.opExtrude","CAP_FACE",FACE,{"disambiguationData":[OSD([sQuery(id+"F0.wireOp",EDGE,"E0"),sQuery(id+"F0.wireOp",EDGE,"E1"),sQuery(id+"F0.wireOp",EDGE,"E2"),sQuery(id+"F0.wireOp",EDGE,"E3"),sQuery(id+"F0.wireOp",EDGE,"E4"),sQuery(id+"F0.wireOp",EDGE,"E5"),sQuery(id+"F0.wireOp",EDGE,"E6"),sQuery(id+"F0.wireOp",EDGE,"E7"),sQuery(id+"F0.wireOp",EDGE,"E8"),sQuery(id+"F0.wireOp",EDGE,"E9"),sQuery(id+"F0.wireOp",EDGE,"E10"),sQuery(id+"F0.wireOp",EDGE,"E11"),sQuery(id+"F0.wireOp",EDGE,"E12"),sQuery(id+"F0.wireOp",EDGE,"E13"),sQuery(id+"F0.wireOp",EDGE,"E14"),sQuery(id+"F0.wireOp",EDGE,"E15"),sQuery(id+"F0.wireOp",EDGE,"E16"),sQuery(id+"F0.wireOp",EDGE,"E17"),sQuery(id+"F0.wireOp",EDGE,"E18"),sQuery(id+"F0.wireOp",EDGE,"E19"),sQuery(id+"F0.wireOp",EDGE,"E20"),sQuery(id+"F0.wireOp",EDGE,"E21"),sQuery(id+"F0.wireOp",EDGE,"E22"),sQuery(id+"F0.wireOp",EDGE,"E23"),sQuery(id+"F0.wireOp",EDGE,"E24"),sQuery(id+"F0.wireOp",EDGE,"E25"),sQuery(id+"F0.wireOp",EDGE,"E26"),sQuery(id+"F0.wireOp",EDGE,"E27"),sQuery(id+"F0.wireOp",EDGE,"E28"),sQuery(id+"F0.wireOp",EDGE,"E29"),sQuery(id+"F0.wireOp",EDGE,"E30"),sQuery(id+"F0.wireOp",EDGE,"E31"),sQuery(id+"F0.wireOp",EDGE,"E32"),sQuery(id+"F0.wireOp",EDGE,"E33"),sQuery(id+"F0.wireOp",EDGE,"E34"),sQuery(id+"F0.wireOp",EDGE,"E35"),sQuery(id+"F0.wireOp",EDGE,"E36"),sQuery(id+"F0.wireOp",EDGE,"E37"),sQuery(id+"F0.wireOp",EDGE,"E38"),sQuery(id+"F0.wireOp",EDGE,"E39"),sQuery(id+"F0.wireOp",EDGE,"E40"),sQuery(id+"F0.wireOp",EDGE,"E41"),sQuery(id+"F0.wireOp",EDGE,"E42"),sQuery(id+"F0.wireOp",EDGE,"E43"),sQuery(id+"F0.wireOp",EDGE,"E44"),sQuery(id+"F0.wireOp",EDGE,"E45"),sQuery(id+"F0.wireOp",EDGE,"E46"),sQuery(id+"F0.wireOp",EDGE,"E47"),sQuery(id+"F0.wireOp",EDGE,"E48"),sQuery(id+"F0.wireOp",EDGE,"E49"),sQuery(id+"F0.wireOp",EDGE,"E50"),sQuery(id+"F0.wireOp",EDGE,"E51"),sQuery(id+"F0.wireOp",EDGE,"E52"),sQuery(id+"F0.wireOp",EDGE,"E53"),sQuery(id+"F0.wireOp",EDGE,"E54"),sQuery(id+"F0.wireOp",EDGE,"E55"),sQuery(id+"F0.wireOp",EDGE,"E56"),sQuery(id+"F0.wireOp",EDGE,"E57"),sQuery(id+"F0.wireOp",EDGE,"E58"),sQuery(id+"F0.wireOp",EDGE,"E59"),sQuery(id+"F0.wireOp",EDGE,"E60"),sQuery(id+"F0.wireOp",EDGE,"E61"),sQuery(id+"F0.wireOp",EDGE,"E62"),sQuery(id+"F0.wireOp",EDGE,"E63"),sQuery(id+"F0.wireOp",EDGE,"E64"),sQuery(id+"F0.wireOp",EDGE,"E65"),sQuery(id+"F0.wireOp",EDGE,"E66"),sQuery(id+"F0.wireOp",EDGE,"E67"),sQuery(id+"F0.wireOp",EDGE,"E68"),sQuery(id+"F0.wireOp",EDGE,"E69"),sQuery(id+"F0.wireOp",EDGE,"E70"),sQuery(id+"F0.wireOp",EDGE,"E71"),sQuery(id+"F0.wireOp",EDGE,"E72"),sQuery(id+"F0.wireOp",EDGE,"E73"),sQuery(id+"F0.wireOp",EDGE,"E74"),sQuery(id+"F0.wireOp",EDGE,"E75"),sQuery(id+"F0.wireOp",EDGE,"E76"),sQuery(id+"F0.wireOp",EDGE,"E77"),sQuery(id+"F0.wireOp",EDGE,"E78"),sQuery(id+"F0.wireOp",EDGE,"E79"),sQuery(id+"F0.wireOp",EDGE,"E80"),sQuery(id+"F0.wireOp",EDGE,"E81"),sQuery(id+"F0.wireOp",EDGE,"E82"),sQuery(id+"F0.wireOp",EDGE,"E83"),sQuery(id+"F0.wireOp",EDGE,"E84"),sQuery(id+"F0.wireOp",EDGE,"E85"),sQuery(id+"F0.wireOp",EDGE,"E86"),sQuery(id+"F0.wireOp",EDGE,"E87"),sQuery(id+"F0.wireOp",EDGE,"E88"),sQuery(id+"F0.wireOp",EDGE,"E89"),sQuery(id+"F0.wireOp",EDGE,"E90"),sQuery(id+"F0.wireOp",EDGE,"E91"),sQuery(id+"F0.wireOp",EDGE,"E92"),sQuery(id+"F0.wireOp",EDGE,"E93"),sQuery(id+"F0.wireOp",EDGE,"E94"),sQuery(id+"F0.wireOp",EDGE,"E95"),sQuery(id+"F0.wireOp",EDGE,"E96"),sQuery(id+"F0.wireOp",EDGE,"E97"),sQuery(id+"F0.wireOp",EDGE,"E98"),sQuery(id+"F0.wireOp",EDGE,"E99"),sQuery(id+"F0.wireOp",EDGE,"E100"),sQuery(id+"F0.wireOp",EDGE,"E101"),sQuery(id+"F0.wireOp",EDGE,"E102"),sQuery(id+"F0.wireOp",EDGE,"E103"),sQuery(id+"F0.wireOp",EDGE,"E104"),sQuery(id+"F0.wireOp",EDGE,"E105"),sQuery(id+"F0.wireOp",EDGE,"E106"),sQuery(id+"F0.wireOp",EDGE,"E107"),sQuery(id+"F0.wireOp",EDGE,"E108"),sQuery(id+"F0.wireOp",EDGE,"E109"),sQuery(id+"F0.wireOp",EDGE,"E110"),sQuery(id+"F0.wireOp",EDGE,"E111"),sQuery(id+"F0.wireOp",EDGE,"E112"),sQuery(id+"F0.wireOp",EDGE,"E113"),sQuery(id+"F0.wireOp",EDGE,"E114"),sQuery(id+"F0.wireOp",EDGE,"E115"),sQuery(id+"F0.wireOp",EDGE,"E116"),sQuery(id+"F0.wireOp",EDGE,"E117"),sQuery(id+"F0.wireOp",EDGE,"E118"),sQuery(id+"F0.wireOp",EDGE,"E119"),sQuery(id+"F0.wireOp",EDGE,"E120"),sQuery(id+"F0.wireOp",EDGE,"E121"),sQuery(id+"F0.wireOp",EDGE,"E122"),sQuery(id+"F0.wireOp",EDGE,"E123")])],"isStart":false});
            var sketch = newSketch(context, id + "F6", { "sketchPlane" : qUnion([Q0])});
            skLineSegment(sketch, "E327", {"start": v(107.15, -47.15) * mm, "end": v(94.15, -34.15) * mm});
            skSolve(sketch);
        }
        {
            var Q0;
            Q0=makeQuery(id+"F6.imprint","IMPRINT",FACE,{"disambiguationData":[TD([[makeQuery(id+"F6.imprint","IMPRINT",EDGE,{"derivedFrom":sQuery(id+"F6.wireOp",EDGE,"E327")}),1.0]])]});
            extrude(context, id + "F7", {"entities" : qUnion([Q0]), "operationType" : NewBodyOperationType.ADD, "depth" : 5 * mm});
        }
    });
